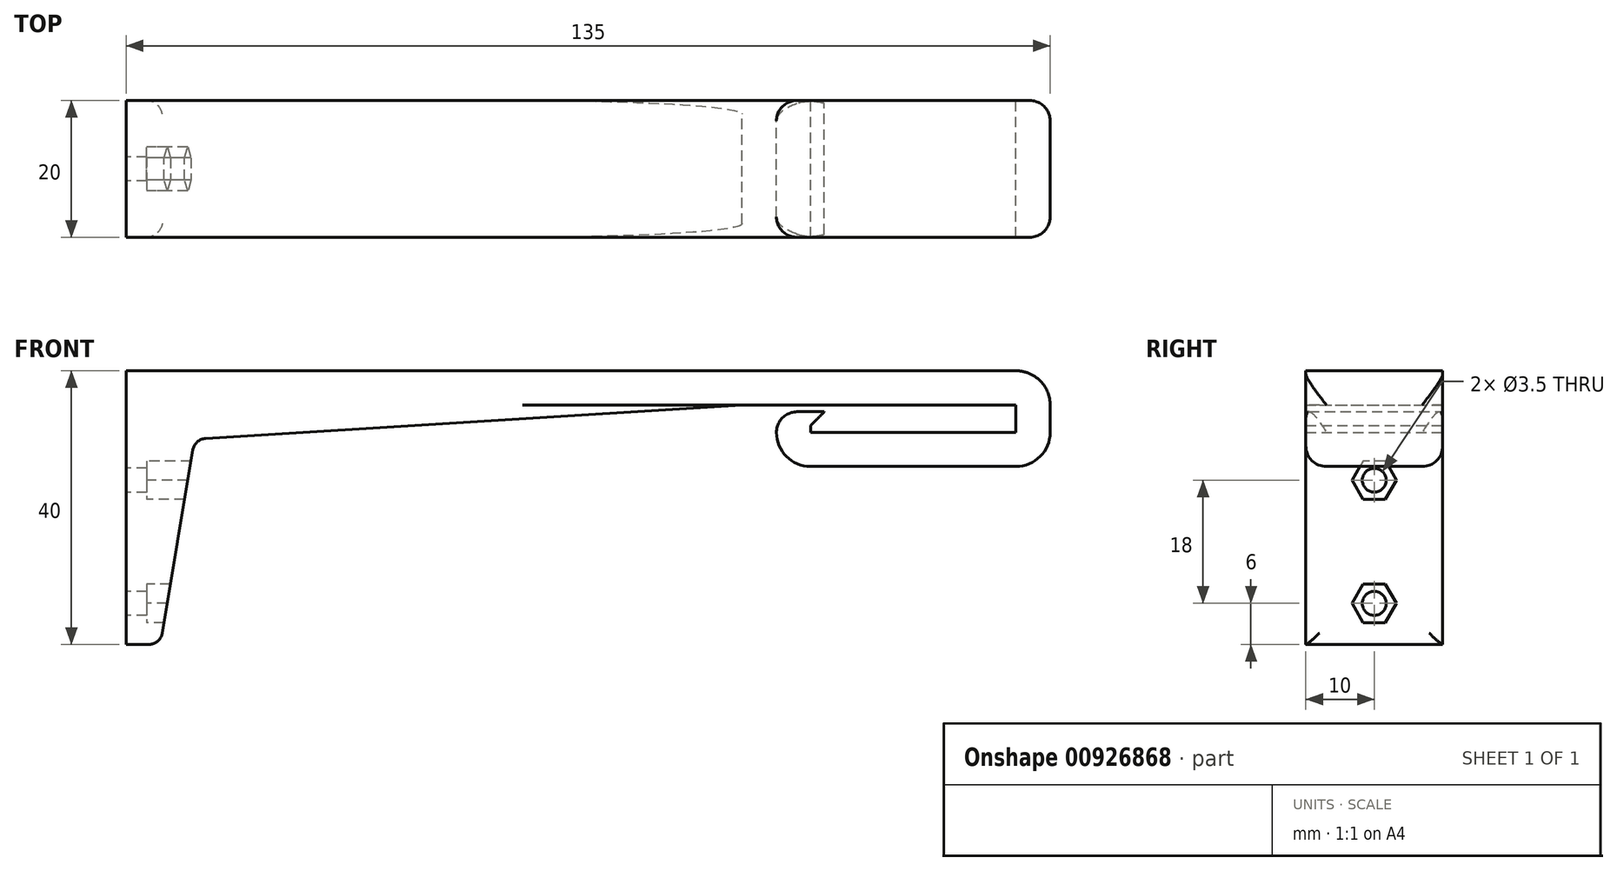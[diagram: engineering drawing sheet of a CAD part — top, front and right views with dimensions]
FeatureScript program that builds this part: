
annotation { "Feature Type Name" : "Feature", "Feature Type Description" : "" }
export const myFeature = defineFeature(function(context is Context, id is Id, definition is map)
    precondition{}
    {
        {
            var Q0;
            Q0=qCreatedBy(makeId("Front.planeOp"),FACE);
            var sketch = newSketch(context, id + "F0", { "sketchPlane" : qUnion([Q0])});
            skLineSegment(sketch, "E0", {"start": v(0, 0) * mm, "end": v(0, 40) * mm});
            skLineSegment(sketch, "E1", {"start": v(0, 40) * mm, "end": v(130, 40) * mm});
            skLineSegment(sketch, "E2", {"start": v(135, 35) * mm, "end": v(135, 31) * mm});
            skLineSegment(sketch, "E3", {"start": v(130, 26) * mm, "end": v(100, 26) * mm});
            skLineSegment(sketch, "E4", {"start": v(95, 31) * mm, "end": v(95, 34) * mm});
            skLineSegment(sketch, "E5", {"start": v(100, 32) * mm, "end": v(100, 31) * mm});
            skLineSegment(sketch, "E6", {"start": v(100, 31) * mm, "end": v(130, 31) * mm});
            skLineSegment(sketch, "E7", {"start": v(130, 31) * mm, "end": v(130, 35) * mm});
            skLineSegment(sketch, "E8", {"start": v(130, 35) * mm, "end": v(90, 35) * mm});
            skLineSegment(sketch, "E9", {"start": v(5, 0) * mm, "end": v(0, 0) * mm});
            skLineSegment(sketch, "E10", {"start": v(90, 35) * mm, "end": v(10, 30) * mm});
            skLineSegment(sketch, "E11", {"start": v(10, 30) * mm, "end": v(5, 0) * mm});
            skLineSegment(sketch, "E12", {"start": v(100, 32) * mm, "end": v(102, 34) * mm});
            skLineSegment(sketch, "E13", {"start": v(95, 34) * mm, "end": v(102, 34) * mm});
            skPoint(sketch, "E14.visualSharp", {"position": v(135, 40) * mm});
            skArc(sketch, "E14.filletArc", {"start": v(135, 35) * mm, "mid": v(133.54, 38.54) * mm, "end": v(130, 40) * mm});
            skPoint(sketch, "E15.visualSharp", {"position": v(135, 26) * mm});
            skArc(sketch, "E15.filletArc", {"start": v(130, 26) * mm, "mid": v(133.54, 27.46) * mm, "end": v(135, 31) * mm});
            skPoint(sketch, "E16.visualSharp", {"position": v(95, 26) * mm});
            skArc(sketch, "E16.filletArc", {"start": v(95, 31) * mm, "mid": v(96.46, 27.46) * mm, "end": v(100, 26) * mm});
            skSolve(sketch);
        }
        {
            var Q0;
            Q0 = qSketchRegion(id + "F0", true);
            extrude(context, id + "F1", {"entities" : qUnion([Q0]), "depth" : 20 * mm, "offsetDistance" : 25 * mm});
        }
        {
            var Q0;
            Q0=makeQuery(id+"F1.opExtrude","SWEPT_FACE",FACE,{"disambiguationData":[OSD([sQuery(id+"F0.wireOp",EDGE,"E0")])]});
            var sketch = newSketch(context, id + "F2", { "sketchPlane" : qUnion([Q0])});
            skLineSegment(sketch, "E17", {"start": v(10, 0) * mm, "end": v(10, 40) * mm, "construction": true});
            skCircle(sketch, "E18", {"center": v(10, 6) * mm, "radius": 1.75 * mm});
            skCircle(sketch, "E19", {"center": v(10, 24) * mm, "radius": 1.75 * mm});
            skSolve(sketch);
        }
        {
            var Q0;
            Q0 = qSketchRegion(id + "F2", true);
            var Q1;
            Q1=makeQuery(id+"F1.opExtrude","SWEPT_FACE",FACE,{"disambiguationData":[OSD([sQuery(id+"F0.wireOp",EDGE,"E11")])]});
            extrude(context, id + "F3", {"entities" : qUnion([Q0]), "operationType" : NewBodyOperationType.REMOVE, "endBound" : BoundingType.UP_TO_SURFACE, "oppositeDirection" : true, "depth" : 25 * mm, "endBoundEntityFace" : qUnion([Q1]), "offsetDistance" : 25 * mm});
        }
        {
            var Q0;
            Q0=makeQuery(id+"F1.opExtrude","SWEPT_FACE",FACE,{"disambiguationData":[OSD([sQuery(id+"F0.wireOp",EDGE,"E0")])]});
            cPlane(context, id + "F4", {"entities" : qUnion([Q0]), "cplaneType" : CPlaneType.OFFSET, "offset" : 3 * mm, "oppositeDirection" : true, "width" : 150 * mm, "height" : 150 * mm});
        }
        {
            var Q0;
            Q0=qCreatedBy(id+"F4.planeOp",FACE);
            var sketch = newSketch(context, id + "F5", { "sketchPlane" : qUnion([Q0])});
            skCircle(sketch, "E20.cCircle", {"center": v(10, 24) * mm, "radius": 2.8 * mm, "construction": true});
            skLineSegment(sketch, "E20.0", {"start": v(11.62, 26.8) * mm, "end": v(13.23, 24) * mm});
            skLineSegment(sketch, "E20.1", {"start": v(13.23, 24) * mm, "end": v(11.62, 21.2) * mm});
            skLineSegment(sketch, "E20.2", {"start": v(11.62, 21.2) * mm, "end": v(8.38, 21.2) * mm});
            skLineSegment(sketch, "E20.3", {"start": v(8.38, 21.2) * mm, "end": v(6.77, 24) * mm});
            skLineSegment(sketch, "E20.4", {"start": v(6.77, 24) * mm, "end": v(8.38, 26.8) * mm});
            skLineSegment(sketch, "E20.5", {"start": v(8.38, 26.8) * mm, "end": v(11.62, 26.8) * mm});
            skPoint(sketch, "E20.0.midPoint", {"position": v(12.42, 25.4) * mm});
            skCircle(sketch, "E21.cCircle", {"center": v(10, 6) * mm, "radius": 2.8 * mm, "construction": true});
            skLineSegment(sketch, "E21.0", {"start": v(11.62, 8.8) * mm, "end": v(13.23, 6) * mm});
            skLineSegment(sketch, "E21.1", {"start": v(13.23, 6) * mm, "end": v(11.62, 3.2) * mm});
            skLineSegment(sketch, "E21.2", {"start": v(11.62, 3.2) * mm, "end": v(8.38, 3.2) * mm});
            skLineSegment(sketch, "E21.3", {"start": v(8.38, 3.2) * mm, "end": v(6.77, 6) * mm});
            skLineSegment(sketch, "E21.4", {"start": v(6.77, 6) * mm, "end": v(8.38, 8.8) * mm});
            skLineSegment(sketch, "E21.5", {"start": v(8.38, 8.8) * mm, "end": v(11.62, 8.8) * mm});
            skPoint(sketch, "E21.0.midPoint", {"position": v(12.42, 7.4) * mm});
            skSolve(sketch);
        }
        {
            var Q0;
            Q0 = qSketchRegion(id + "F5", true);
            var Q1;
            Q1=makeQuery(id+"F1.opExtrude","SWEPT_FACE",FACE,{"disambiguationData":[OSD([sQuery(id+"F0.wireOp",EDGE,"E11")])]});
            extrude(context, id + "F6", {"entities" : qUnion([Q0]), "operationType" : NewBodyOperationType.REMOVE, "endBound" : BoundingType.UP_TO_SURFACE, "oppositeDirection" : true, "depth" : 25 * mm, "endBoundEntityFace" : qUnion([Q1]), "offsetDistance" : 25 * mm});
        }
        {
            var Q0;
            Q0=makeQuery(id+"F1.opExtrude","SWEPT_EDGE",EDGE,{"disambiguationData":[OSD([sQuery(id+"F0.wireOp",EDGE,"E4"),sQuery(id+"F0.wireOp",EDGE,"E13")])]});
            fillet(context, id + "F7", {"entities" : qUnion([Q0]), "radius" : 3 * mm, "tangentPropagation" : true, "allowEdgeOverflow" : false});
        }
        {
            var Q0;
            Q0=makeQuery(id+"F1.opExtrude","CAP_EDGE",EDGE,{"disambiguationData":[OSD([sQuery(id+"F0.wireOp",EDGE,"E10")])],"isStart":false});
            var Q1;
            Q1=makeQuery(id+"F1.opExtrude","CAP_EDGE",EDGE,{"disambiguationData":[OSD([sQuery(id+"F0.wireOp",EDGE,"E11")])],"isStart":false});
            var Q2;
            Q2=makeQuery(id+"F1.opExtrude","SWEPT_EDGE",EDGE,{"disambiguationData":[OSD([sQuery(id+"F0.wireOp",EDGE,"E9"),sQuery(id+"F0.wireOp",EDGE,"E11")])]});
            var Q3;
            Q3=makeQuery(id+"F1.opExtrude","CAP_EDGE",EDGE,{"disambiguationData":[OSD([sQuery(id+"F0.wireOp",EDGE,"E11")])],"isStart":true});
            var Q4;
            Q4=makeQuery(id+"F1.opExtrude","CAP_EDGE",EDGE,{"disambiguationData":[OSD([sQuery(id+"F0.wireOp",EDGE,"E10")])],"isStart":true});
            var Q5;
            Q5=makeQuery(id+"F1.opExtrude","SWEPT_EDGE",EDGE,{"disambiguationData":[OSD([sQuery(id+"F0.wireOp",EDGE,"E10"),sQuery(id+"F0.wireOp",EDGE,"E11")])]});
            fillet(context, id + "F8", {"entities" : qUnion([Q0, Q1, Q2, Q3, Q4, Q5]), "radius" : 2 * mm, "tangentPropagation" : true, "allowEdgeOverflow" : false});
        }
        {
            var Q0;
            Q0=makeQuery(id+"F1.opExtrude","CAP_EDGE",EDGE,{"disambiguationData":[OSD([sQuery(id+"F0.wireOp",EDGE,"E16.filletArc")])],"isStart":false});
            var Q1;
            Q1=makeQuery(id+"F1.opExtrude","CAP_EDGE",EDGE,{"disambiguationData":[OSD([sQuery(id+"F0.wireOp",EDGE,"E3")])],"isStart":false});
            var Q2;
            Q2=makeQuery(id+"F1.opExtrude","CAP_EDGE",EDGE,{"disambiguationData":[OSD([sQuery(id+"F0.wireOp",EDGE,"E15.filletArc")])],"isStart":false});
            var Q3;
            Q3=makeQuery(id+"F1.opExtrude","CAP_EDGE",EDGE,{"disambiguationData":[OSD([sQuery(id+"F0.wireOp",EDGE,"E2")])],"isStart":false});
            var Q4;
            Q4=makeQuery(id+"F1.opExtrude","CAP_EDGE",EDGE,{"disambiguationData":[OSD([sQuery(id+"F0.wireOp",EDGE,"E16.filletArc")])],"isStart":true});
            var Q5;
            Q5=makeQuery(id+"F1.opExtrude","CAP_EDGE",EDGE,{"disambiguationData":[OSD([sQuery(id+"F0.wireOp",EDGE,"E3")])],"isStart":true});
            var Q6;
            Q6=makeQuery(id+"F1.opExtrude","CAP_EDGE",EDGE,{"disambiguationData":[OSD([sQuery(id+"F0.wireOp",EDGE,"E15.filletArc")])],"isStart":true});
            var Q7;
            Q7=makeQuery(id+"F1.opExtrude","CAP_EDGE",EDGE,{"disambiguationData":[OSD([sQuery(id+"F0.wireOp",EDGE,"E2")])],"isStart":true});
            fillet(context, id + "F9", {"entities" : qUnion([Q0, Q1, Q2, Q3, Q4, Q5, Q6, Q7]), "radius" : 3 * mm, "allowEdgeOverflow" : false});
        }
    });
